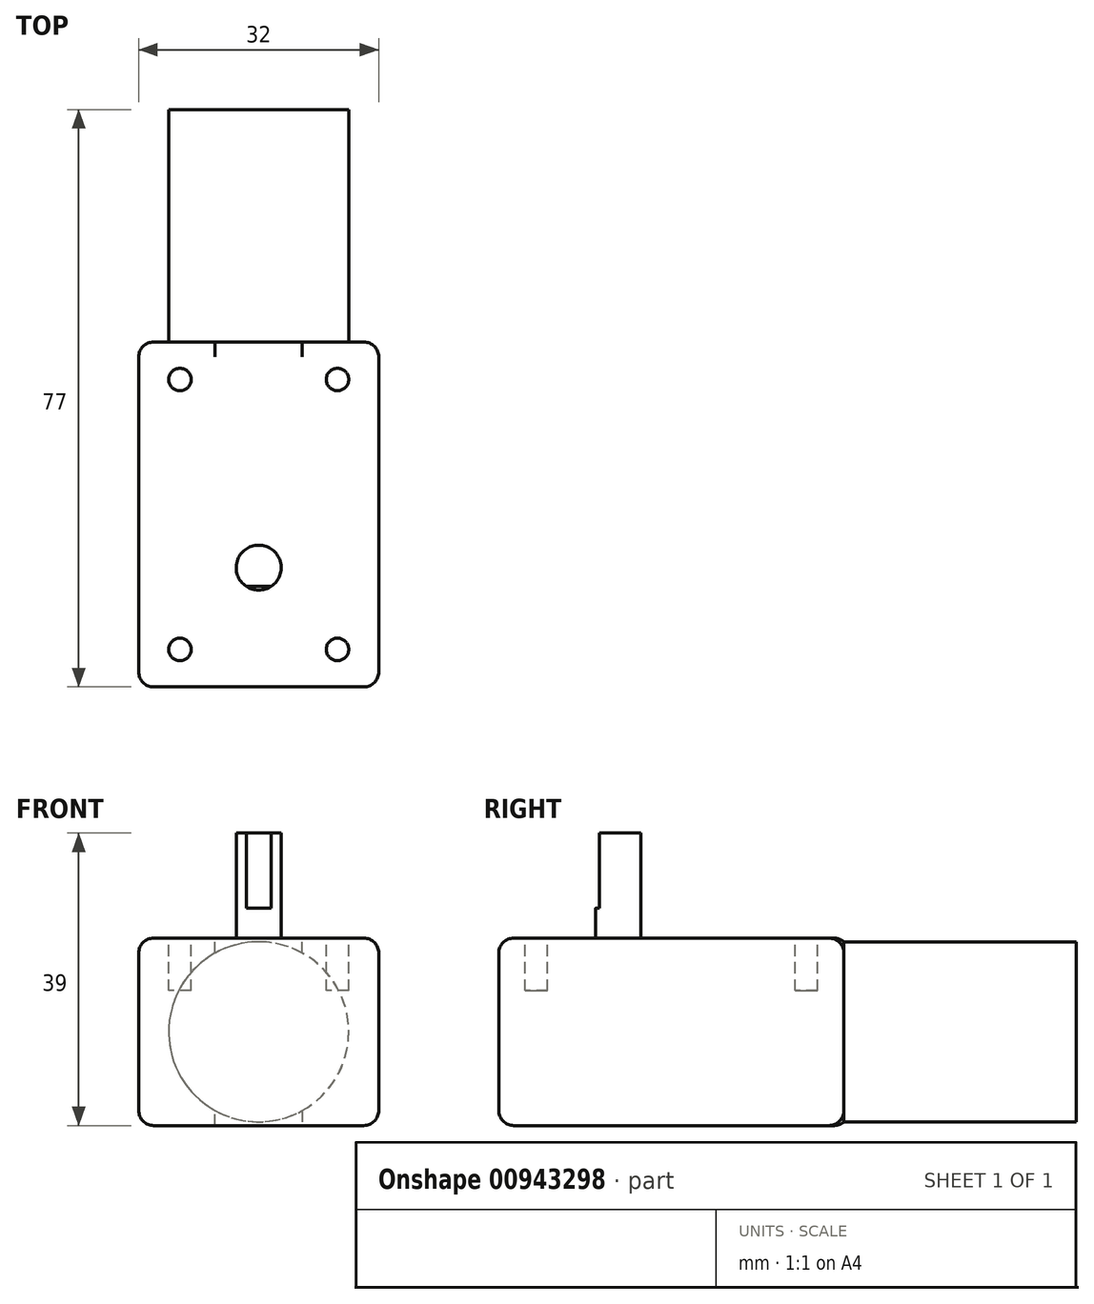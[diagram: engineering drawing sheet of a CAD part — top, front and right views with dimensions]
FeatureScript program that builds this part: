
annotation { "Feature Type Name" : "Feature", "Feature Type Description" : "" }
export const myFeature = defineFeature(function(context is Context, id is Id, definition is map)
    precondition{}
    {
        {
            var Q0;
            Q0=qCreatedBy(makeId("Front.planeOp"),FACE);
            var sketch = newSketch(context, id + "F0", { "sketchPlane" : qUnion([Q0])});
            skLineSegment(sketch, "E0.bottom", {"start": v(0, 0) * mm, "end": v(32, 0) * mm});
            skLineSegment(sketch, "E0.top", {"start": v(0, 25) * mm, "end": v(32, 25) * mm});
            skLineSegment(sketch, "E0.left", {"start": v(0, 0) * mm, "end": v(0, 25) * mm});
            skLineSegment(sketch, "E0.right", {"start": v(32, 0) * mm, "end": v(32, 25) * mm});
            skSolve(sketch);
        }
        {
            var Q0;
            Q0 = qSketchRegion(id + "F0", true);
            extrude(context, id + "F1", {"entities" : qUnion([Q0]), "depth" : 46 * mm, "offsetDistance" : 25 * mm});
        }
        {
            var Q0;
            Q0=makeQuery(id+"F1.opExtrude","CAP_FACE",FACE,{"disambiguationData":[OSD([sQuery(id+"F0.wireOp",EDGE,"E0.bottom"),sQuery(id+"F0.wireOp",EDGE,"E0.top"),sQuery(id+"F0.wireOp",EDGE,"E0.left"),sQuery(id+"F0.wireOp",EDGE,"E0.right")])],"isStart":true});
            var sketch = newSketch(context, id + "F2", { "sketchPlane" : qUnion([Q0])});
            skLineSegment(sketch, "E1", {"start": v(-32, 25) * mm, "end": v(0, 0) * mm, "construction": true});
            skLineSegment(sketch, "E2", {"start": v(0, 25) * mm, "end": v(-32, 0) * mm, "construction": true});
            skCircle(sketch, "E3", {"center": v(-16, 12.5) * mm, "radius": 12 * mm});
            skSolve(sketch);
        }
        {
            var Q0;
            Q0 = qSketchRegion(id + "F2", true);
            extrude(context, id + "F3", {"entities" : qUnion([Q0]), "operationType" : NewBodyOperationType.ADD, "depth" : 31 * mm, "offsetDistance" : 25 * mm});
        }
        {
            var Q0;
            Q0=makeQuery(id+"F1.opExtrude","SWEPT_FACE",FACE,{"disambiguationData":[OSD([sQuery(id+"F0.wireOp",EDGE,"E0.top")])]});
            var sketch = newSketch(context, id + "F4", { "sketchPlane" : qUnion([Q0])});
            skLineSegment(sketch, "E4", {"start": v(0, -23) * mm, "end": v(32, -23) * mm, "construction": true});
            skLineSegment(sketch, "E5", {"start": v(16, -46) * mm, "end": v(16, 0) * mm, "construction": true});
            skCircle(sketch, "E6", {"center": v(5.5, -41) * mm, "radius": 1.5 * mm});
            skCircle(sketch, "E7.MirrorC", {"center": v(5.5, -5) * mm, "radius": 1.5 * mm});
            skCircle(sketch, "E8.MirrorC", {"center": v(26.5, -41) * mm, "radius": 1.5 * mm});
            skCircle(sketch, "E9.MirrorC", {"center": v(26.5, -5) * mm, "radius": 1.5 * mm});
            skSolve(sketch);
        }
        {
            var Q0;
            Q0 = qSketchRegion(id + "F4", true);
            extrude(context, id + "F5", {"entities" : qUnion([Q0]), "operationType" : NewBodyOperationType.REMOVE, "oppositeDirection" : true, "depth" : 7 * mm, "offsetDistance" : 25 * mm});
        }
        {
            var Q0;
            Q0=makeQuery(id+"F1.opExtrude","SWEPT_FACE",FACE,{"disambiguationData":[OSD([sQuery(id+"F0.wireOp",EDGE,"E0.top")])]});
            var sketch = newSketch(context, id + "F6", { "sketchPlane" : qUnion([Q0])});
            skCircle(sketch, "E10", {"center": v(16, -30.09) * mm, "radius": 3 * mm});
            skLineSegment(sketch, "E11", {"start": v(16, -46) * mm, "end": v(16, 0) * mm, "construction": true});
            skSolve(sketch);
        }
        {
            var Q0;
            Q0 = qSketchRegion(id + "F6", true);
            extrude(context, id + "F7", {"entities" : qUnion([Q0]), "operationType" : NewBodyOperationType.ADD, "depth" : 14 * mm, "offsetDistance" : 25 * mm});
        }
        {
            var Q0;
            Q0=makeQuery(id+"F7.opExtrude","CAP_FACE",FACE,{"disambiguationData":[OSD([sQuery(id+"F6.wireOp",EDGE,"E10")])],"isStart":false});
            var sketch = newSketch(context, id + "F8", { "sketchPlane" : qUnion([Q0])});
            skLineSegment(sketch, "E12", {"start": v(14.34, -32.59) * mm, "end": v(17.66, -32.59) * mm});
            skLineSegment(sketch, "E13", {"start": v(17.66, -32.59) * mm, "end": v(17.66, -33.09) * mm});
            skLineSegment(sketch, "E14", {"start": v(17.66, -33.09) * mm, "end": v(14.34, -33.09) * mm});
            skLineSegment(sketch, "E15", {"start": v(14.34, -33.09) * mm, "end": v(14.34, -32.59) * mm});
            skSolve(sketch);
        }
        {
            var Q0;
            Q0 = qSketchRegion(id + "F8", true);
            extrude(context, id + "F9", {"entities" : qUnion([Q0]), "operationType" : NewBodyOperationType.REMOVE, "oppositeDirection" : true, "depth" : 10 * mm, "offsetDistance" : 25 * mm});
        }
        {
            var Q0;
            Q0=makeQuery(id+"F1.opExtrude","CAP_EDGE",EDGE,{"disambiguationData":[OSD([sQuery(id+"F0.wireOp",EDGE,"E0.top")])],"isStart":false});
            var Q1;
            Q1=makeQuery(id+"F1.opExtrude","SWEPT_EDGE",EDGE,{"disambiguationData":[OSD([sQuery(id+"F0.wireOp",EDGE,"E0.top"),sQuery(id+"F0.wireOp",EDGE,"E0.right")])]});
            var Q2;
            Q2=makeQuery(id+"F1.opExtrude","CAP_EDGE",EDGE,{"disambiguationData":[OSD([sQuery(id+"F0.wireOp",EDGE,"E0.right")])],"isStart":false});
            var Q3;
            Q3=makeQuery(id+"F1.opExtrude","SWEPT_EDGE",EDGE,{"disambiguationData":[OSD([sQuery(id+"F0.wireOp",EDGE,"E0.top"),sQuery(id+"F0.wireOp",EDGE,"E0.left")])]});
            var Q4;
            Q4=makeQuery(id+"F1.opExtrude","CAP_EDGE",EDGE,{"disambiguationData":[OSD([sQuery(id+"F0.wireOp",EDGE,"E0.left")])],"isStart":false});
            var Q5;
            Q5=makeQuery(id+"F1.opExtrude","CAP_EDGE",EDGE,{"disambiguationData":[OSD([sQuery(id+"F0.wireOp",EDGE,"E0.bottom")])],"isStart":false});
            var Q6;
            Q6=makeQuery(id+"F1.opExtrude","SWEPT_EDGE",EDGE,{"disambiguationData":[OSD([sQuery(id+"F0.wireOp",EDGE,"E0.bottom"),sQuery(id+"F0.wireOp",EDGE,"E0.left")])]});
            var Q7;
            Q7=makeQuery(id+"F1.opExtrude","SWEPT_EDGE",EDGE,{"disambiguationData":[OSD([sQuery(id+"F0.wireOp",EDGE,"E0.bottom"),sQuery(id+"F0.wireOp",EDGE,"E0.right")])]});
            var Q8;
            Q8=makeQuery(id+"F1.opExtrude","CAP_EDGE",EDGE,{"disambiguationData":[OSD([sQuery(id+"F0.wireOp",EDGE,"E0.bottom")])],"isStart":true});
            var Q9;
            Q9=makeQuery(id+"F1.opExtrude","CAP_EDGE",EDGE,{"disambiguationData":[OSD([sQuery(id+"F0.wireOp",EDGE,"E0.top")])],"isStart":true});
            var Q10;
            Q10=makeQuery(id+"F1.opExtrude","CAP_EDGE",EDGE,{"disambiguationData":[OSD([sQuery(id+"F0.wireOp",EDGE,"E0.left")])],"isStart":true});
            var Q11;
            Q11=makeQuery(id+"F1.opExtrude","CAP_EDGE",EDGE,{"disambiguationData":[OSD([sQuery(id+"F0.wireOp",EDGE,"E0.right")])],"isStart":true});
            fillet(context, id + "F10", {"entities" : qUnion([Q0, Q1, Q2, Q3, Q4, Q5, Q6, Q7, Q8, Q9, Q10, Q11]), "radius" : 2 * mm, "tangentPropagation" : true, "allowEdgeOverflow" : false});
        }
    });
